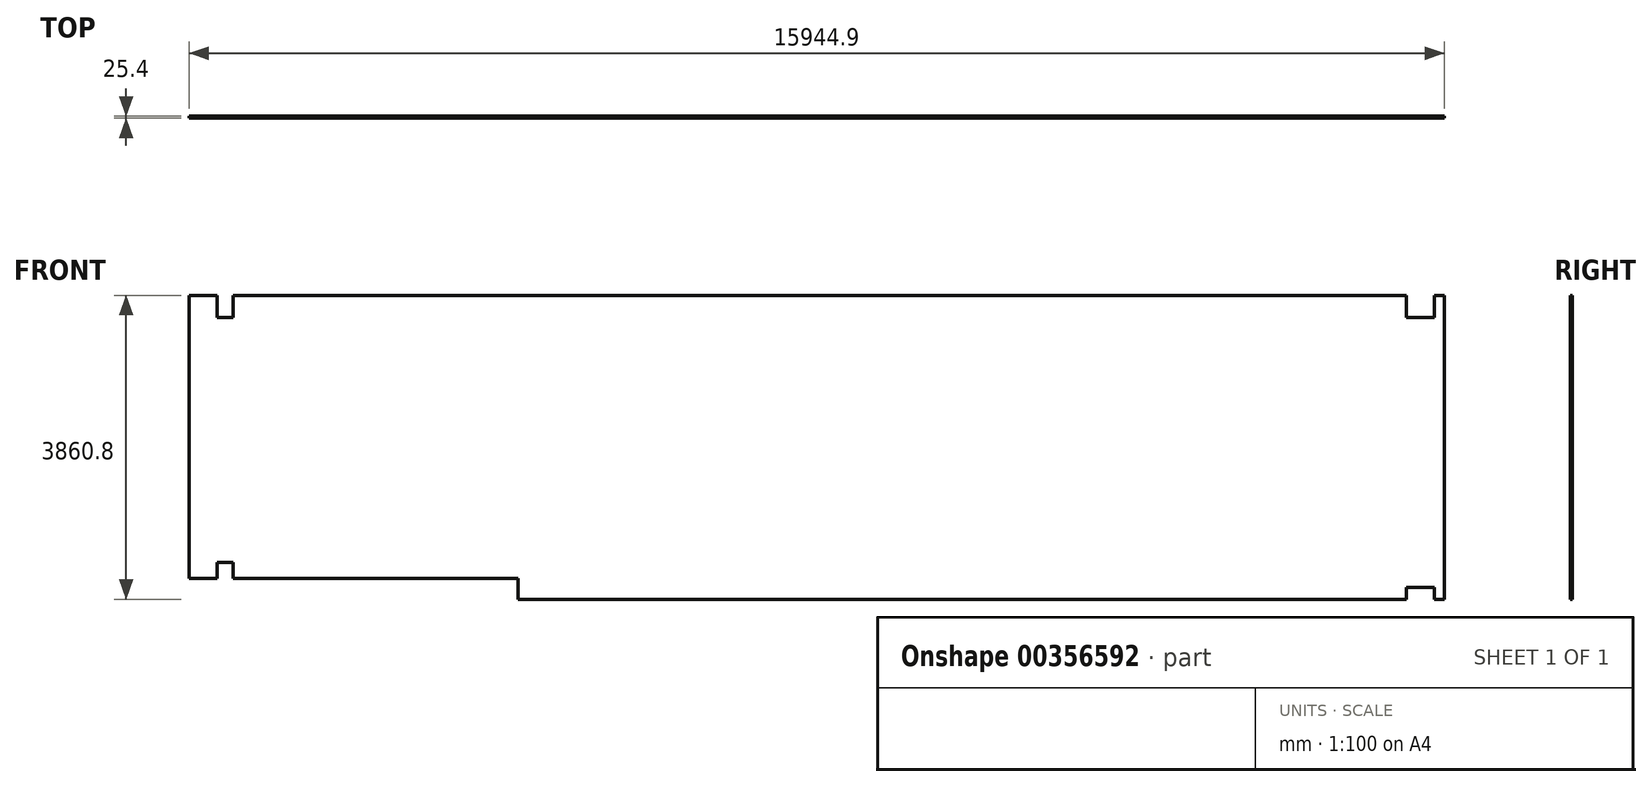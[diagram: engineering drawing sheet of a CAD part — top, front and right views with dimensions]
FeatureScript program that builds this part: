
annotation { "Feature Type Name" : "Feature", "Feature Type Description" : "" }
export const myFeature = defineFeature(function(context is Context, id is Id, definition is map)
    precondition{}
    {
        {
            var Q0;
            Q0=qCreatedBy(makeId("Front.planeOp"),FACE);
            var sketch = newSketch(context, id + "F0", { "sketchPlane" : qUnion([Q0])});
            skLineSegment(sketch, "E0.top", {"start": v(0, 3860.8) * mm, "end": v(355.6, 3860.8) * mm});
            skLineSegment(sketch, "E0.left", {"start": v(0, 266.7) * mm, "end": v(0, 3860.8) * mm});
            skLineSegment(sketch, "E0.right", {"start": v(15944.85, 0) * mm, "end": v(15944.85, 3860.8) * mm});
            skLineSegment(sketch, "E1", {"start": v(0, 266.7) * mm, "end": v(355.6, 266.7) * mm});
            skLineSegment(sketch, "E2", {"start": v(4178.3, 266.7) * mm, "end": v(4178.3, 0) * mm});
            skLineSegment(sketch, "E3", {"start": v(355.6, 266.7) * mm, "end": v(355.6, 469.9) * mm});
            skLineSegment(sketch, "E4", {"start": v(355.6, 469.9) * mm, "end": v(558.8, 469.9) * mm});
            skLineSegment(sketch, "E5", {"start": v(558.8, 469.9) * mm, "end": v(558.8, 266.7) * mm});
            skLineSegment(sketch, "E6.trimOffspring", {"start": v(558.8, 266.7) * mm, "end": v(4178.3, 266.7) * mm});
            skLineSegment(sketch, "E7", {"start": v(355.6, 3860.8) * mm, "end": v(355.6, 3581.4) * mm});
            skLineSegment(sketch, "E8", {"start": v(355.6, 3581.4) * mm, "end": v(558.8, 3581.4) * mm});
            skLineSegment(sketch, "E9", {"start": v(558.8, 3581.4) * mm, "end": v(558.8, 3860.8) * mm});
            skLineSegment(sketch, "E10.trimOffspring", {"start": v(558.8, 3860.8) * mm, "end": v(15462.25, 3860.8) * mm});
            skLineSegment(sketch, "E11", {"start": v(15462.25, 3860.8) * mm, "end": v(15462.25, 3581.4) * mm});
            skLineSegment(sketch, "E12", {"start": v(15462.25, 3581.4) * mm, "end": v(15817.85, 3581.4) * mm});
            skLineSegment(sketch, "E13", {"start": v(15817.85, 3581.4) * mm, "end": v(15817.85, 3860.8) * mm});
            skLineSegment(sketch, "E14.trimOffspring", {"start": v(15817.85, 3860.8) * mm, "end": v(15944.85, 3860.8) * mm});
            skLineSegment(sketch, "E15", {"start": v(15462.25, 0) * mm, "end": v(15462.25, 152.4) * mm});
            skLineSegment(sketch, "E16", {"start": v(15462.25, 152.4) * mm, "end": v(15817.85, 152.4) * mm});
            skLineSegment(sketch, "E17", {"start": v(15817.85, 152.4) * mm, "end": v(15817.85, 0) * mm});
            skLineSegment(sketch, "E18.trimOffspring", {"start": v(15817.85, 0) * mm, "end": v(15944.85, 0) * mm});
            skLineSegment(sketch, "E19", {"start": v(4178.3, 0) * mm, "end": v(15462.25, 0) * mm});
            skSolve(sketch);
        }
        {
            var Q0;
            Q0 = qSketchRegion(id + "F0", true);
            extrude(context, id + "F1", {"entities" : qUnion([Q0]), "depth" : 25.4 * mm});
        }
    });
